# Revit family: SH-1811 TOOKAR
name_source: partatom
category: Lighting Fixtures
revit_build: Autodesk Revit 2017 (Build: 20160225_1515(x64)
units: mm (PartAtom-declared; Revit-internal decimal feet)

## family parameters
Cut with Voids When Loaded = No
Host = Face
Light Source = No
Part Type = Normal
Room Calculation Point = No
Round Connector Dimension = Use Diameter
Shared = Yes

## types (4) — shared parameters
Body Material = Aluminum
Cutout width = 10.5 cm
Default Elevation = 121.9 cm
Flicker = Free Flicker
IP = IP4X
Lamp = LED
Manufacturer = SHOA
Protection Class = Class I
Type medule = SMD-DOB
Voltage/Frequency = 230v/50hz
Width = 12.0 cm
color rendering index(CRI) = 80
color temperature = 4000K
consumption current = 0 A
cutout Depth = 4.0 cm
instalation = Recessed ceiling
wattage = 50 W
website = www.shoaco.com

## per-type parameters (varying)
| type | Connector L | Count | Description | Light Linear | Linear | Model | URL | body color | light L connector |
| Sh-1811-Reccsed(Black color-4000K-LED) | No | 0 | چراغ با طول نیم متر قابل سفارش می باشد | Yes | Yes | Sh-1811-Tookar | https://www.shoaco.com | Black Body | No |
| Sh-1811-Reccsed(White color-4000K-LED) | No | 0 |  | Yes | Yes | Sh-1811-Tookar | https://www.shoaco.com | White Body | No |
| Sh-1811-Reccsed-L connector(White color-4000K-LED) | Yes | 1 |  | No | No | Sh-1811-Tookar-L connector |  | White Body | Yes |
| Sh-1811-Reccsed-L connector(Black color-4000K-LED) | Yes | 1 |  | No | No | Sh-1811-Tookar-L connector |  | Black Body | Yes |

## geometry (parser evidence)
native form markers: Sweep x4
no freeform markers — native parametric forms only
